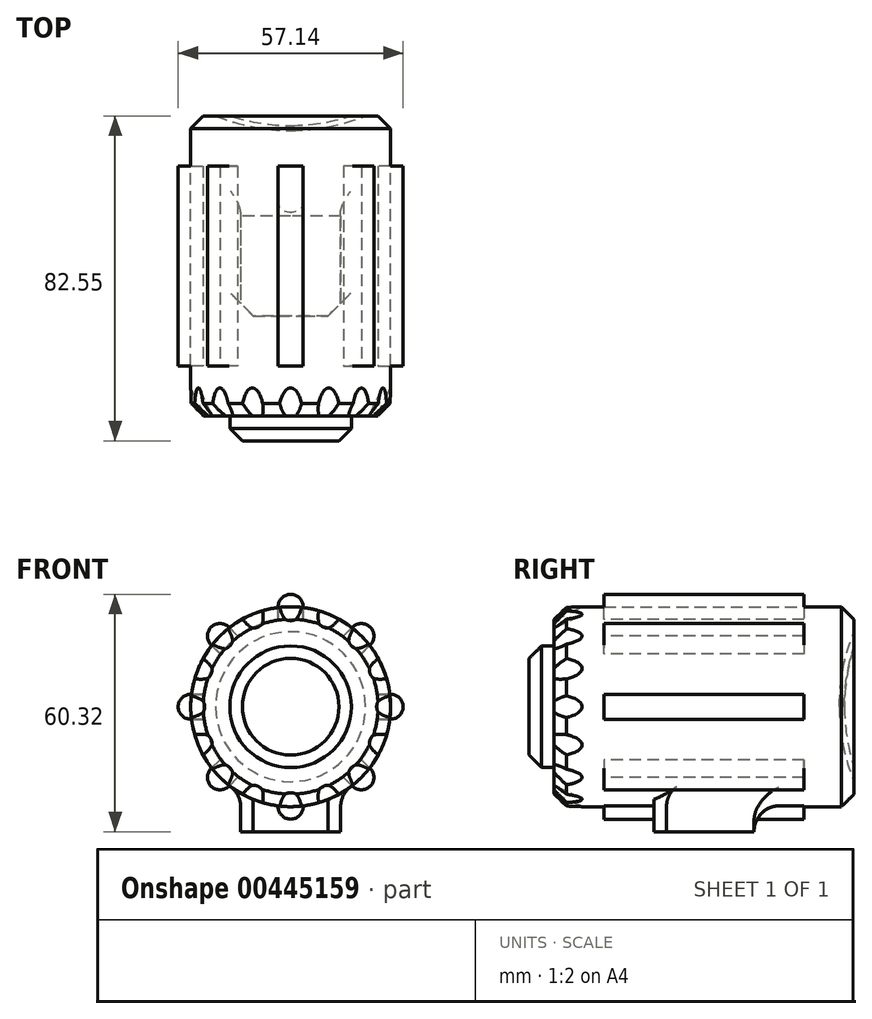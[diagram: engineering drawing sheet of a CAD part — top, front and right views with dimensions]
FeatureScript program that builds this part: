
annotation { "Feature Type Name" : "Feature", "Feature Type Description" : "" }
export const myFeature = defineFeature(function(context is Context, id is Id, definition is map)
    precondition{}
    {
        {
            var Q0;
            Q0=qCreatedBy(makeId("Front.planeOp"),FACE);
            var sketch = newSketch(context, id + "F0", { "sketchPlane" : qUnion([Q0])});
            skCircle(sketch, "E0", {"center": v(0, 0) * mm, "radius": 25.4 * mm});
            skSolve(sketch);
        }
        {
            var Q0;
            Q0=makeQuery(id+"F0.imprint","IMPRINT",FACE,{"disambiguationData":[TD([[makeQuery(id+"F0.imprint","IMPRINT",EDGE,{"derivedFrom":sQuery(id+"F0.wireOp",EDGE,"E0")}),1.0]])]});
            extrude(context, id + "F1", {"entities" : qUnion([Q0]), "depth" : 76.2 * mm});
        }
        {
            var Q0;
            Q0=qCreatedBy(makeId("Right.planeOp"),FACE);
            var sketch = newSketch(context, id + "F2", { "sketchPlane" : qUnion([Q0])});
            skLineSegment(sketch, "E1", {"start": v(-76.2, 25.4) * mm, "end": v(0, 25.4) * mm});
            skLineSegment(sketch, "E2", {"start": v(0, -25.4) * mm, "end": v(-76.2, -25.4) * mm});
            skLineSegment(sketch, "E3", {"start": v(0, 0) * mm, "end": v(0, 22.23) * mm});
            skLineSegment(sketch, "E4", {"start": v(0, 22.23) * mm, "end": v(-3.18, 25.4) * mm});
            skLineSegment(sketch, "E5", {"start": v(0, 0) * mm, "end": v(-8.41, 0) * mm});
            skLineSegment(sketch, "E6", {"start": v(0, 22.23) * mm, "end": v(0, 25.4) * mm});
            skSolve(sketch);
        }
        {
            var Q0;
            {var subQ2=sQuery(id+"F2.wireOp",EDGE,"E4");Q0=makeQuery(id+"F2.imprint","IMPRINT",FACE,{"disambiguationData":[TD([[makeQuery(id+"F2.imprint","IMPRINT",EDGE,{"derivedFrom":subQ2}),-1.0]])]});}
            var Q1;
            Q1=sQuery(id+"F2.wireOp",EDGE,"E5");
            revolve(context, id + "F3", {"operationType" : NewBodyOperationType.REMOVE, "entities" : qUnion([Q0]), "axis" : qUnion([Q1]), "revolveType" : RevolveType.FULL, "oppositeDirection" : true});
        }
        {
            var Q0;
            Q0=qCreatedBy(makeId("Right.planeOp"),FACE);
            var sketch = newSketch(context, id + "F4", { "sketchPlane" : qUnion([Q0])});
            skLineSegment(sketch, "E7", {"start": v(0, 0) * mm, "end": v(-127, 0) * mm});
            skLineSegment(sketch, "E8", {"start": v(-76.2, 25.4) * mm, "end": v(-3.18, 25.4) * mm});
            skLineSegment(sketch, "E9", {"start": v(-127, 0) * mm, "end": v(-76.2, 25.4) * mm});
            skLineSegment(sketch, "E10", {"start": v(-76.2, 25.4) * mm, "end": v(-74.78, 22.56) * mm});
            skLineSegment(sketch, "E11", {"start": v(-74.78, 22.56) * mm, "end": v(-119.9, 0) * mm});
            skLineSegment(sketch, "E12", {"start": v(-74.78, 22.56) * mm, "end": v(-62.33, 28.78) * mm});
            skLineSegment(sketch, "E13", {"start": v(-62.33, 28.78) * mm, "end": v(-63.75, 31.62) * mm});
            skLineSegment(sketch, "E14", {"start": v(-63.75, 31.62) * mm, "end": v(-76.2, 25.4) * mm});
            skSolve(sketch);
        }
        {
            var Q0;
            {var subQ0=sQuery(id+"F4.wireOp",EDGE,"E9");Q0=makeQuery(id+"F4.imprint","IMPRINT",FACE,{"disambiguationData":[TD([[makeQuery(id+"F4.imprint","IMPRINT",EDGE,{"derivedFrom":subQ0}),-1.0]])]});}
            var Q1;
            {var subQ4=sQuery(id+"F4.wireOp",EDGE,"E13");Q1=makeQuery(id+"F4.imprint","IMPRINT",FACE,{"disambiguationData":[TD([[makeQuery(id+"F4.imprint","IMPRINT",EDGE,{"derivedFrom":subQ4}),1.0]])]});}
            var Q2;
            {var subQ0=sQuery(id+"F4.wireOp",EDGE,"E10");Q2=makeQuery(id+"F4.imprint","IMPRINT",FACE,{"disambiguationData":[TD([[makeQuery(id+"F4.imprint","IMPRINT",EDGE,{"derivedFrom":subQ0}),1.0]])]});}
            var Q3;
            Q3=sQuery(id+"F4.wireOp",EDGE,"E9");
            revolve(context, id + "F5", {"entities" : qUnion([Q0, Q1, Q2]), "axis" : qUnion([Q3]), "revolveType" : RevolveType.FULL, "oppositeDirection" : true});
        }
        {
            var Q0;
            Q0=makeQuery(id+"F5.opRevolve","SWEPT_BODY",BODY,{"disambiguationData":[OSD([sQuery(id+"F4.wireOp",EDGE,"E7"),sQuery(id+"F4.wireOp",EDGE,"E9"),sQuery(id+"F4.wireOp",EDGE,"E11"),sQuery(id+"F4.wireOp",EDGE,"E12"),sQuery(id+"F4.wireOp",EDGE,"E13"),sQuery(id+"F4.wireOp",EDGE,"E14")])]});
            var Q1;
            Q1=sQuery(id+"F4.wireOp",EDGE,"E7");
            circularPattern(context, id + "F6", {"operationType" : NewBodyOperationType.REMOVE, "entities" : qUnion([Q0]), "axis" : qUnion([Q1]), "angle" : 360 * degree, "instanceCount" : 16, "equalSpace" : true});
        }
        {
            var Q0;
            Q0=qCreatedBy(makeId("Right.planeOp"),FACE);
            var sketch = newSketch(context, id + "F7", { "sketchPlane" : qUnion([Q0])});
            skLineSegment(sketch, "E15", {"start": v(-3.18, 25.4) * mm, "end": v(0, 22.23) * mm});
            skLineSegment(sketch, "E16", {"start": v(0, -22.23) * mm, "end": v(-3.18, -25.4) * mm});
            skLineSegment(sketch, "E17", {"start": v(0, 22.23) * mm, "end": v(0, 19.05) * mm});
            skArc(sketch, "E18", {"start": v(0, 19.05) * mm, "mid": v(-3.7, 0) * mm, "end": v(0, -19.05) * mm});
            skLineSegment(sketch, "E19", {"start": v(0, -22.23) * mm, "end": v(0, -19.05) * mm});
            skLineSegment(sketch, "E20", {"start": v(0, 19.05) * mm, "end": v(0, -19.05) * mm});
            skLineSegment(sketch, "E21", {"start": v(0, 0) * mm, "end": v(-2.47, 0) * mm});
            skLineSegment(sketch, "E22", {"start": v(0, 19.05) * mm, "end": v(5.56, 19.05) * mm});
            skLineSegment(sketch, "E23", {"start": v(5.56, 19.05) * mm, "end": v(5.56, -19.05) * mm});
            skLineSegment(sketch, "E24", {"start": v(5.56, -19.05) * mm, "end": v(0, -19.05) * mm});
            skLineSegment(sketch, "E25", {"start": v(-3.7, 0) * mm, "end": v(5.56, 0) * mm});
            skSolve(sketch);
        }
        {
            var Q0;
            {var subQ3=sQuery(id+"F7.wireOp",EDGE,"E25");var subQ6=makeQuery(id+"F7.imprint","IMPRINT",VERTEX,{"derivedFrom":subQ3});Q0=makeQuery(id+"F7.imprint","IMPRINT",FACE,{"disambiguationData":[TD([[makeQuery(id+"F7.imprint","IMPRINT",EDGE,{"disambiguationData":[TD([[subQ6,1.0]])],"derivedFrom":subQ3}),1.0]])]});}
            var Q1;
            {var subQ0=sQuery(id+"F7.wireOp",EDGE,"E22");Q1=makeQuery(id+"F7.imprint","IMPRINT",FACE,{"disambiguationData":[TD([[makeQuery(id+"F7.imprint","IMPRINT",EDGE,{"derivedFrom":subQ0}),-1.0]])]});}
            var Q2;
            Q2=sQuery(id+"F7.wireOp",EDGE,"E25");
            revolve(context, id + "F8", {"operationType" : NewBodyOperationType.REMOVE, "entities" : qUnion([Q0, Q1]), "axis" : qUnion([Q2]), "revolveType" : RevolveType.FULL, "oppositeDirection" : true});
        }
        {
            var Q0;
            Q0=qCreatedBy(makeId("Right.planeOp"),FACE);
            var sketch = newSketch(context, id + "F9", { "sketchPlane" : qUnion([Q0])});
            skLineSegment(sketch, "E26.0", {"start": v(0, 19.05) * mm, "end": v(0, -19.05) * mm});
            skArc(sketch, "E27", {"start": v(0, 19.05) * mm, "mid": v(-3.7, 0) * mm, "end": v(0, -19.05) * mm});
            skArc(sketch, "E28", {"start": v(0, 15.35) * mm, "mid": v(-2.44, 0) * mm, "end": v(0, -15.35) * mm});
            skLineSegment(sketch, "E29", {"start": v(0, 19.05) * mm, "end": v(0, 15.35) * mm});
            skLineSegment(sketch, "E30", {"start": v(0, -19.05) * mm, "end": v(0, -15.35) * mm});
            skLineSegment(sketch, "E31", {"start": v(0, 0) * mm, "end": v(-3.7, 0) * mm});
            skArc(sketch, "E32", {"start": v(-0.15, 14.89) * mm, "mid": v(-0.04, 15.36) * mm, "end": v(0, 15.84) * mm});
            skSolve(sketch);
        }
        {
            var Q0;
            {var subQ5=sQuery(id+"F9.wireOp",EDGE,"E32");Q0=makeQuery(id+"F9.imprint","IMPRINT",FACE,{"disambiguationData":[TD([[makeQuery(id+"F9.imprint","IMPRINT",EDGE,{"derivedFrom":subQ5}),1.0]])]});}
            var Q1;
            Q1=sQuery(id+"F9.wireOp",EDGE,"E31");
            revolve(context, id + "F10", {"entities" : qUnion([Q0]), "axis" : qUnion([Q1]), "revolveType" : RevolveType.FULL});
        }
        {
            var Q0;
            {var subQ0=sQuery(id+"F0.wireOp",EDGE,"E0");var subQ1=makeQuery(id+"F5.opRevolve","SWEPT_FACE",FACE,{"disambiguationData":[OSD([sQuery(id+"F4.wireOp",EDGE,"E11"),sQuery(id+"F4.wireOp",EDGE,"E12")])]});Q0=makeQuery(id+"F6.boolean.opBoolean","SPLIT",EDGE,{"disambiguationData":[TD([makeQuery(id+"F1.opExtrude","SWEPT_FACE",FACE,{"disambiguationData":[OSD([subQ0])]}),makeQuery(id+"F1.opExtrude","CAP_FACE",FACE,{"disambiguationData":[OSD([subQ0])],"isStart":false}),makeQuery(id+"F6.opPattern","COPY",FACE,{"derivedFrom":subQ1,"instanceName":"13"}),makeQuery(id+"F6.opPattern","COPY",FACE,{"derivedFrom":subQ1,"instanceName":"14"})])],"derivedFrom":makeQuery(id+"F1.opExtrude","CAP_EDGE",EDGE,{"disambiguationData":[OSD([subQ0])],"isStart":false})});}
            var Q1;
            {var subQ0=sQuery(id+"F0.wireOp",EDGE,"E0");var subQ1=makeQuery(id+"F5.opRevolve","SWEPT_FACE",FACE,{"disambiguationData":[OSD([sQuery(id+"F4.wireOp",EDGE,"E11"),sQuery(id+"F4.wireOp",EDGE,"E12")])]});Q1=makeQuery(id+"F6.boolean.opBoolean","SPLIT",EDGE,{"disambiguationData":[TD([makeQuery(id+"F1.opExtrude","SWEPT_FACE",FACE,{"disambiguationData":[OSD([subQ0])]}),makeQuery(id+"F1.opExtrude","CAP_FACE",FACE,{"disambiguationData":[OSD([subQ0])],"isStart":false}),makeQuery(id+"F6.opPattern","COPY",FACE,{"derivedFrom":subQ1,"instanceName":"12"}),makeQuery(id+"F6.opPattern","COPY",FACE,{"derivedFrom":subQ1,"instanceName":"13"})])],"derivedFrom":makeQuery(id+"F1.opExtrude","CAP_EDGE",EDGE,{"disambiguationData":[OSD([subQ0])],"isStart":false})});}
            var Q2;
            {var subQ0=sQuery(id+"F0.wireOp",EDGE,"E0");var subQ1=makeQuery(id+"F5.opRevolve","SWEPT_FACE",FACE,{"disambiguationData":[OSD([sQuery(id+"F4.wireOp",EDGE,"E11"),sQuery(id+"F4.wireOp",EDGE,"E12")])]});Q2=makeQuery(id+"F6.boolean.opBoolean","SPLIT",EDGE,{"disambiguationData":[TD([makeQuery(id+"F1.opExtrude","SWEPT_FACE",FACE,{"disambiguationData":[OSD([subQ0])]}),makeQuery(id+"F1.opExtrude","CAP_FACE",FACE,{"disambiguationData":[OSD([subQ0])],"isStart":false}),makeQuery(id+"F6.opPattern","COPY",FACE,{"derivedFrom":subQ1,"instanceName":"11"}),makeQuery(id+"F6.opPattern","COPY",FACE,{"derivedFrom":subQ1,"instanceName":"12"})])],"derivedFrom":makeQuery(id+"F1.opExtrude","CAP_EDGE",EDGE,{"disambiguationData":[OSD([subQ0])],"isStart":false})});}
            var Q3;
            {var subQ0=sQuery(id+"F0.wireOp",EDGE,"E0");var subQ1=makeQuery(id+"F5.opRevolve","SWEPT_FACE",FACE,{"disambiguationData":[OSD([sQuery(id+"F4.wireOp",EDGE,"E11"),sQuery(id+"F4.wireOp",EDGE,"E12")])]});Q3=makeQuery(id+"F6.boolean.opBoolean","SPLIT",EDGE,{"disambiguationData":[TD([makeQuery(id+"F1.opExtrude","SWEPT_FACE",FACE,{"disambiguationData":[OSD([subQ0])]}),makeQuery(id+"F1.opExtrude","CAP_FACE",FACE,{"disambiguationData":[OSD([subQ0])],"isStart":false}),makeQuery(id+"F6.opPattern","COPY",FACE,{"derivedFrom":subQ1,"instanceName":"10"}),makeQuery(id+"F6.opPattern","COPY",FACE,{"derivedFrom":subQ1,"instanceName":"11"})])],"derivedFrom":makeQuery(id+"F1.opExtrude","CAP_EDGE",EDGE,{"disambiguationData":[OSD([subQ0])],"isStart":false})});}
            var Q4;
            {var subQ0=sQuery(id+"F0.wireOp",EDGE,"E0");var subQ1=makeQuery(id+"F5.opRevolve","SWEPT_FACE",FACE,{"disambiguationData":[OSD([sQuery(id+"F4.wireOp",EDGE,"E11"),sQuery(id+"F4.wireOp",EDGE,"E12")])]});Q4=makeQuery(id+"F6.boolean.opBoolean","SPLIT",EDGE,{"disambiguationData":[TD([makeQuery(id+"F1.opExtrude","SWEPT_FACE",FACE,{"disambiguationData":[OSD([subQ0])]}),makeQuery(id+"F1.opExtrude","CAP_FACE",FACE,{"disambiguationData":[OSD([subQ0])],"isStart":false}),makeQuery(id+"F6.opPattern","COPY",FACE,{"derivedFrom":subQ1,"instanceName":"9"}),makeQuery(id+"F6.opPattern","COPY",FACE,{"derivedFrom":subQ1,"instanceName":"10"})])],"derivedFrom":makeQuery(id+"F1.opExtrude","CAP_EDGE",EDGE,{"disambiguationData":[OSD([subQ0])],"isStart":false})});}
            var Q5;
            {var subQ0=sQuery(id+"F0.wireOp",EDGE,"E0");var subQ1=makeQuery(id+"F5.opRevolve","SWEPT_FACE",FACE,{"disambiguationData":[OSD([sQuery(id+"F4.wireOp",EDGE,"E11"),sQuery(id+"F4.wireOp",EDGE,"E12")])]});Q5=makeQuery(id+"F6.boolean.opBoolean","SPLIT",EDGE,{"disambiguationData":[TD([makeQuery(id+"F1.opExtrude","SWEPT_FACE",FACE,{"disambiguationData":[OSD([subQ0])]}),makeQuery(id+"F1.opExtrude","CAP_FACE",FACE,{"disambiguationData":[OSD([subQ0])],"isStart":false}),makeQuery(id+"F6.opPattern","COPY",FACE,{"derivedFrom":subQ1,"instanceName":"8"}),makeQuery(id+"F6.opPattern","COPY",FACE,{"derivedFrom":subQ1,"instanceName":"9"})])],"derivedFrom":makeQuery(id+"F1.opExtrude","CAP_EDGE",EDGE,{"disambiguationData":[OSD([subQ0])],"isStart":false})});}
            var Q6;
            {var subQ0=sQuery(id+"F0.wireOp",EDGE,"E0");var subQ1=makeQuery(id+"F5.opRevolve","SWEPT_FACE",FACE,{"disambiguationData":[OSD([sQuery(id+"F4.wireOp",EDGE,"E11"),sQuery(id+"F4.wireOp",EDGE,"E12")])]});Q6=makeQuery(id+"F6.boolean.opBoolean","SPLIT",EDGE,{"disambiguationData":[TD([makeQuery(id+"F1.opExtrude","SWEPT_FACE",FACE,{"disambiguationData":[OSD([subQ0])]}),makeQuery(id+"F1.opExtrude","CAP_FACE",FACE,{"disambiguationData":[OSD([subQ0])],"isStart":false}),makeQuery(id+"F6.opPattern","COPY",FACE,{"derivedFrom":subQ1,"instanceName":"7"}),makeQuery(id+"F6.opPattern","COPY",FACE,{"derivedFrom":subQ1,"instanceName":"8"})])],"derivedFrom":makeQuery(id+"F1.opExtrude","CAP_EDGE",EDGE,{"disambiguationData":[OSD([subQ0])],"isStart":false})});}
            var Q7;
            {var subQ0=sQuery(id+"F0.wireOp",EDGE,"E0");var subQ1=makeQuery(id+"F5.opRevolve","SWEPT_FACE",FACE,{"disambiguationData":[OSD([sQuery(id+"F4.wireOp",EDGE,"E11"),sQuery(id+"F4.wireOp",EDGE,"E12")])]});Q7=makeQuery(id+"F6.boolean.opBoolean","SPLIT",EDGE,{"disambiguationData":[TD([makeQuery(id+"F1.opExtrude","SWEPT_FACE",FACE,{"disambiguationData":[OSD([subQ0])]}),makeQuery(id+"F1.opExtrude","CAP_FACE",FACE,{"disambiguationData":[OSD([subQ0])],"isStart":false}),makeQuery(id+"F6.opPattern","COPY",FACE,{"derivedFrom":subQ1,"instanceName":"6"}),makeQuery(id+"F6.opPattern","COPY",FACE,{"derivedFrom":subQ1,"instanceName":"7"})])],"derivedFrom":makeQuery(id+"F1.opExtrude","CAP_EDGE",EDGE,{"disambiguationData":[OSD([subQ0])],"isStart":false})});}
            var Q8;
            {var subQ0=sQuery(id+"F0.wireOp",EDGE,"E0");var subQ1=makeQuery(id+"F5.opRevolve","SWEPT_FACE",FACE,{"disambiguationData":[OSD([sQuery(id+"F4.wireOp",EDGE,"E11"),sQuery(id+"F4.wireOp",EDGE,"E12")])]});Q8=makeQuery(id+"F6.boolean.opBoolean","SPLIT",EDGE,{"disambiguationData":[TD([makeQuery(id+"F1.opExtrude","SWEPT_FACE",FACE,{"disambiguationData":[OSD([subQ0])]}),makeQuery(id+"F1.opExtrude","CAP_FACE",FACE,{"disambiguationData":[OSD([subQ0])],"isStart":false}),makeQuery(id+"F6.opPattern","COPY",FACE,{"derivedFrom":subQ1,"instanceName":"5"}),makeQuery(id+"F6.opPattern","COPY",FACE,{"derivedFrom":subQ1,"instanceName":"6"})])],"derivedFrom":makeQuery(id+"F1.opExtrude","CAP_EDGE",EDGE,{"disambiguationData":[OSD([subQ0])],"isStart":false})});}
            var Q9;
            {var subQ0=sQuery(id+"F0.wireOp",EDGE,"E0");var subQ1=makeQuery(id+"F5.opRevolve","SWEPT_FACE",FACE,{"disambiguationData":[OSD([sQuery(id+"F4.wireOp",EDGE,"E11"),sQuery(id+"F4.wireOp",EDGE,"E12")])]});Q9=makeQuery(id+"F6.boolean.opBoolean","SPLIT",EDGE,{"disambiguationData":[TD([makeQuery(id+"F1.opExtrude","SWEPT_FACE",FACE,{"disambiguationData":[OSD([subQ0])]}),makeQuery(id+"F1.opExtrude","CAP_FACE",FACE,{"disambiguationData":[OSD([subQ0])],"isStart":false}),makeQuery(id+"F6.opPattern","COPY",FACE,{"derivedFrom":subQ1,"instanceName":"4"}),makeQuery(id+"F6.opPattern","COPY",FACE,{"derivedFrom":subQ1,"instanceName":"5"})])],"derivedFrom":makeQuery(id+"F1.opExtrude","CAP_EDGE",EDGE,{"disambiguationData":[OSD([subQ0])],"isStart":false})});}
            var Q10;
            {var subQ0=sQuery(id+"F0.wireOp",EDGE,"E0");var subQ1=makeQuery(id+"F5.opRevolve","SWEPT_FACE",FACE,{"disambiguationData":[OSD([sQuery(id+"F4.wireOp",EDGE,"E11"),sQuery(id+"F4.wireOp",EDGE,"E12")])]});Q10=makeQuery(id+"F6.boolean.opBoolean","SPLIT",EDGE,{"disambiguationData":[TD([makeQuery(id+"F1.opExtrude","SWEPT_FACE",FACE,{"disambiguationData":[OSD([subQ0])]}),makeQuery(id+"F1.opExtrude","CAP_FACE",FACE,{"disambiguationData":[OSD([subQ0])],"isStart":false}),makeQuery(id+"F6.opPattern","COPY",FACE,{"derivedFrom":subQ1,"instanceName":"3"}),makeQuery(id+"F6.opPattern","COPY",FACE,{"derivedFrom":subQ1,"instanceName":"4"})])],"derivedFrom":makeQuery(id+"F1.opExtrude","CAP_EDGE",EDGE,{"disambiguationData":[OSD([subQ0])],"isStart":false})});}
            var Q11;
            {var subQ0=sQuery(id+"F0.wireOp",EDGE,"E0");var subQ1=makeQuery(id+"F5.opRevolve","SWEPT_FACE",FACE,{"disambiguationData":[OSD([sQuery(id+"F4.wireOp",EDGE,"E11"),sQuery(id+"F4.wireOp",EDGE,"E12")])]});Q11=makeQuery(id+"F6.boolean.opBoolean","SPLIT",EDGE,{"disambiguationData":[TD([makeQuery(id+"F1.opExtrude","SWEPT_FACE",FACE,{"disambiguationData":[OSD([subQ0])]}),makeQuery(id+"F1.opExtrude","CAP_FACE",FACE,{"disambiguationData":[OSD([subQ0])],"isStart":false}),makeQuery(id+"F6.opPattern","COPY",FACE,{"derivedFrom":subQ1,"instanceName":"2"}),makeQuery(id+"F6.opPattern","COPY",FACE,{"derivedFrom":subQ1,"instanceName":"3"})])],"derivedFrom":makeQuery(id+"F1.opExtrude","CAP_EDGE",EDGE,{"disambiguationData":[OSD([subQ0])],"isStart":false})});}
            var Q12;
            {var subQ0=sQuery(id+"F0.wireOp",EDGE,"E0");var subQ1=makeQuery(id+"F5.opRevolve","SWEPT_FACE",FACE,{"disambiguationData":[OSD([sQuery(id+"F4.wireOp",EDGE,"E11"),sQuery(id+"F4.wireOp",EDGE,"E12")])]});Q12=makeQuery(id+"F6.boolean.opBoolean","SPLIT",EDGE,{"disambiguationData":[TD([makeQuery(id+"F1.opExtrude","SWEPT_FACE",FACE,{"disambiguationData":[OSD([subQ0])]}),makeQuery(id+"F1.opExtrude","CAP_FACE",FACE,{"disambiguationData":[OSD([subQ0])],"isStart":false}),makeQuery(id+"F6.opPattern","COPY",FACE,{"derivedFrom":subQ1,"instanceName":"1"}),makeQuery(id+"F6.opPattern","COPY",FACE,{"derivedFrom":subQ1,"instanceName":"2"})])],"derivedFrom":makeQuery(id+"F1.opExtrude","CAP_EDGE",EDGE,{"disambiguationData":[OSD([subQ0])],"isStart":false})});}
            var Q13;
            {var subQ0=sQuery(id+"F0.wireOp",EDGE,"E0");var subQ1=makeQuery(id+"F5.opRevolve","SWEPT_FACE",FACE,{"disambiguationData":[OSD([sQuery(id+"F4.wireOp",EDGE,"E11"),sQuery(id+"F4.wireOp",EDGE,"E12")])]});Q13=makeQuery(id+"F6.boolean.opBoolean","SPLIT",EDGE,{"disambiguationData":[TD([makeQuery(id+"F1.opExtrude","SWEPT_FACE",FACE,{"disambiguationData":[OSD([subQ0])]}),makeQuery(id+"F1.opExtrude","CAP_FACE",FACE,{"disambiguationData":[OSD([subQ0])],"isStart":false}),subQ1,makeQuery(id+"F6.opPattern","COPY",FACE,{"derivedFrom":subQ1,"instanceName":"1"})])],"derivedFrom":makeQuery(id+"F1.opExtrude","CAP_EDGE",EDGE,{"disambiguationData":[OSD([subQ0])],"isStart":false})});}
            var Q14;
            {var subQ0=sQuery(id+"F0.wireOp",EDGE,"E0");var subQ1=makeQuery(id+"F5.opRevolve","SWEPT_FACE",FACE,{"disambiguationData":[OSD([sQuery(id+"F4.wireOp",EDGE,"E11"),sQuery(id+"F4.wireOp",EDGE,"E12")])]});Q14=makeQuery(id+"F6.boolean.opBoolean","SPLIT",EDGE,{"disambiguationData":[TD([makeQuery(id+"F1.opExtrude","SWEPT_FACE",FACE,{"disambiguationData":[OSD([subQ0])]}),makeQuery(id+"F1.opExtrude","CAP_FACE",FACE,{"disambiguationData":[OSD([subQ0])],"isStart":false}),subQ1,makeQuery(id+"F6.opPattern","COPY",FACE,{"derivedFrom":subQ1,"instanceName":"15"})])],"derivedFrom":makeQuery(id+"F1.opExtrude","CAP_EDGE",EDGE,{"disambiguationData":[OSD([subQ0])],"isStart":false})});}
            var Q15;
            {var subQ0=sQuery(id+"F0.wireOp",EDGE,"E0");var subQ1=makeQuery(id+"F5.opRevolve","SWEPT_FACE",FACE,{"disambiguationData":[OSD([sQuery(id+"F4.wireOp",EDGE,"E11"),sQuery(id+"F4.wireOp",EDGE,"E12")])]});Q15=makeQuery(id+"F6.boolean.opBoolean","SPLIT",EDGE,{"disambiguationData":[TD([makeQuery(id+"F1.opExtrude","SWEPT_FACE",FACE,{"disambiguationData":[OSD([subQ0])]}),makeQuery(id+"F1.opExtrude","CAP_FACE",FACE,{"disambiguationData":[OSD([subQ0])],"isStart":false}),makeQuery(id+"F6.opPattern","COPY",FACE,{"derivedFrom":subQ1,"instanceName":"14"}),makeQuery(id+"F6.opPattern","COPY",FACE,{"derivedFrom":subQ1,"instanceName":"15"})])],"derivedFrom":makeQuery(id+"F1.opExtrude","CAP_EDGE",EDGE,{"disambiguationData":[OSD([subQ0])],"isStart":false})});}
            chamfer(context, id + "F11", {"entities" : qUnion([Q0, Q1, Q2, Q3, Q4, Q5, Q6, Q7, Q8, Q9, Q10, Q11, Q12, Q13, Q14, Q15]), "width" : 3.17 * mm, "tangentPropagation" : true});
        }
        {
            var Q0;
            Q0=qCreatedBy(makeId("Right.planeOp"),FACE);
            var sketch = newSketch(context, id + "F12", { "sketchPlane" : qUnion([Q0])});
            skFitSpline(sketch, "E33.0.0", {"points": [v(-76.2, 21.8) * mm, v(-76.2, 20.51) * mm, v(-76.2, 19.23) * mm, v(-76.2, 17.94) * mm]});
            skFitSpline(sketch, "E33.0.7", {"points": [v(-76.2, -21.8) * mm, v(-76.2, -21.16) * mm, v(-76.2, -20.52) * mm, v(-76.2, -19.89) * mm]});
            skFitSpline(sketch, "E33.0.15", {"points": [v(-76.2, 21.8) * mm, v(-76.2, 21.16) * mm, v(-76.2, 20.52) * mm, v(-76.2, 19.89) * mm]});
            skLineSegment(sketch, "E34", {"start": v(-76.2, -21.8) * mm, "end": v(-76.2, 21.8) * mm});
            skLineSegment(sketch, "E35", {"start": v(-76.2, 21.8) * mm, "end": v(-76.2, 15.45) * mm});
            skLineSegment(sketch, "E36", {"start": v(-76.2, -21.8) * mm, "end": v(-76.2, -15.45) * mm});
            skLineSegment(sketch, "E37", {"start": v(-76.2, -15.45) * mm, "end": v(-82.55, -15.45) * mm});
            skLineSegment(sketch, "E38", {"start": v(-76.2, 15.45) * mm, "end": v(-82.55, 15.45) * mm});
            skLineSegment(sketch, "E39", {"start": v(-82.55, 15.45) * mm, "end": v(-82.55, -15.45) * mm});
            skLineSegment(sketch, "E40", {"start": v(-82.55, 0) * mm, "end": v(-76.2, 0) * mm});
            skSolve(sketch);
        }
        {
            var Q0;
            {var subQ0=sQuery(id+"F12.wireOp",EDGE,"E38");Q0=makeQuery(id+"F12.imprint","IMPRINT",FACE,{"disambiguationData":[TD([[makeQuery(id+"F12.imprint","IMPRINT",EDGE,{"derivedFrom":subQ0}),1.0]])]});}
            var Q1;
            Q1=sQuery(id+"F12.wireOp",EDGE,"E40");
            revolve(context, id + "F13", {"entities" : qUnion([Q0]), "axis" : qUnion([Q1]), "revolveType" : RevolveType.FULL});
        }
        {
            var Q0;
            Q0=makeQuery(id+"F13.opRevolve","SWEPT_FACE",FACE,{"disambiguationData":[OSD([sQuery(id+"F12.wireOp",EDGE,"E39")])]});
            chamfer(context, id + "F14", {"entities" : qUnion([Q0]), "width" : 3.17 * mm, "tangentPropagation" : true});
        }
        {
            var Q0;
            Q0=qCreatedBy(makeId("Right.planeOp"),FACE);
            var sketch = newSketch(context, id + "F15", { "sketchPlane" : qUnion([Q0])});
            skLineSegment(sketch, "E41", {"start": v(0, 0) * mm, "end": v(0, 25.4) * mm});
            skLineSegment(sketch, "E42", {"start": v(0, 25.4) * mm, "end": v(-12.7, 25.4) * mm});
            skLineSegment(sketch, "E43", {"start": v(-12.7, 25.4) * mm, "end": v(-12.7, 22.22) * mm});
            skLineSegment(sketch, "E44", {"start": v(-12.7, 22.22) * mm, "end": v(-63.5, 22.22) * mm});
            skLineSegment(sketch, "E45", {"start": v(-63.5, 22.22) * mm, "end": v(-63.5, 28.57) * mm});
            skLineSegment(sketch, "E46", {"start": v(-63.5, 28.57) * mm, "end": v(-12.7, 28.58) * mm});
            skLineSegment(sketch, "E47", {"start": v(-12.7, 28.58) * mm, "end": v(-12.7, 25.4) * mm});
            skSolve(sketch);
        }
        {
            var Q0;
            Q0=makeQuery(id+"F15.imprint","IMPRINT",FACE,{"disambiguationData":[TD([[makeQuery(id+"F15.imprint","IMPRINT",EDGE,{"derivedFrom":sQuery(id+"F15.wireOp",EDGE,"E43")}),-1.0]])]});
            extrude(context, id + "F16", {"entities" : qUnion([Q0]), "endBound" : BoundingType.SYMMETRIC, "depth" : 6.35 * mm});
        }
        {
            var Q0;
            Q0=makeQuery(id+"F16.opExtrude","CAP_EDGE",EDGE,{"disambiguationData":[OSD([sQuery(id+"F15.wireOp",EDGE,"E46")])],"isStart":false});
            var Q1;
            Q1=makeQuery(id+"F16.opExtrude","CAP_EDGE",EDGE,{"disambiguationData":[OSD([sQuery(id+"F15.wireOp",EDGE,"E46")])],"isStart":true});
            fillet(context, id + "F17", {"entities" : qUnion([Q0, Q1]), "radius" : 3.17 * mm, "tangentPropagation" : true, "allowEdgeOverflow" : false});
        }
        {
            var Q0;
            Q0=makeQuery(id+"F16.opExtrude","SWEPT_BODY",BODY,{"disambiguationData":[OSD([sQuery(id+"F15.wireOp",EDGE,"E43"),sQuery(id+"F15.wireOp",EDGE,"E44"),sQuery(id+"F15.wireOp",EDGE,"E45"),sQuery(id+"F15.wireOp",EDGE,"E46"),sQuery(id+"F15.wireOp",EDGE,"E47")])]});
            var Q1;
            Q1=sQuery(id+"F12.wireOp",EDGE,"E40");
            circularPattern(context, id + "F18", {"entities" : qUnion([Q0]), "axis" : qUnion([Q1]), "angle" : 360 * degree, "instanceCount" : 8, "equalSpace" : true});
        }
        {
            var Q0;
            Q0=qCreatedBy(makeId("Right.planeOp"),FACE);
            var sketch = newSketch(context, id + "F19", { "sketchPlane" : qUnion([Q0])});
            skLineSegment(sketch, "E48", {"start": v(0, 0) * mm, "end": v(-25.4, 0) * mm});
            skLineSegment(sketch, "E49", {"start": v(-25.4, 0) * mm, "end": v(-25.4, -31.75) * mm});
            skLineSegment(sketch, "E50", {"start": v(-25.4, -31.75) * mm, "end": v(-50.8, -31.75) * mm});
            skLineSegment(sketch, "E51", {"start": v(-50.8, -31.75) * mm, "end": v(-50.8, 0) * mm});
            skLineSegment(sketch, "E52", {"start": v(-50.8, 0) * mm, "end": v(-25.4, 0) * mm});
            skSolve(sketch);
        }
        {
            var Q0;
            Q0=makeQuery(id+"F19.imprint","IMPRINT",FACE,{"disambiguationData":[TD([[makeQuery(id+"F19.imprint","IMPRINT",EDGE,{"derivedFrom":sQuery(id+"F19.wireOp",EDGE,"E49")}),-1.0]])]});
            extrude(context, id + "F20", {"entities" : qUnion([Q0]), "operationType" : NewBodyOperationType.ADD, "endBound" : BoundingType.SYMMETRIC, "depth" : 25.4 * mm});
        }
        {
            var Q0;
            Q0=makeQuery(id+"F20.opExtrude","CAP_EDGE",EDGE,{"disambiguationData":[OSD([sQuery(id+"F19.wireOp",EDGE,"E51")])],"isStart":true});
            var Q1;
            Q1=makeQuery(id+"F20.opExtrude","CAP_EDGE",EDGE,{"disambiguationData":[OSD([sQuery(id+"F19.wireOp",EDGE,"E51")])],"isStart":false});
            chamfer(context, id + "F21", {"entities" : qUnion([Q0, Q1]), "width" : 3.17 * mm, "tangentPropagation" : true});
        }
        {
            var Q0;
            Q0=makeQuery(id+"F20.boolean.opBoolean","INTERSECT",EDGE,{"derivedFrom":[makeQuery(id+"F1.opExtrude","SWEPT_FACE",FACE,{"disambiguationData":[OSD([sQuery(id+"F0.wireOp",EDGE,"E0")])]}),makeQuery(id+"F20.opExtrude","CAP_FACE",FACE,{"disambiguationData":[OSD([sQuery(id+"F19.wireOp",EDGE,"E49"),sQuery(id+"F19.wireOp",EDGE,"E50"),sQuery(id+"F19.wireOp",EDGE,"E51"),sQuery(id+"F19.wireOp",EDGE,"E52")])],"isStart":false})]});
            var Q1;
            Q1=makeQuery(id+"F20.boolean.opBoolean","INTERSECT",EDGE,{"derivedFrom":[makeQuery(id+"F1.opExtrude","SWEPT_FACE",FACE,{"disambiguationData":[OSD([sQuery(id+"F0.wireOp",EDGE,"E0")])]}),makeQuery(id+"F20.opExtrude","CAP_FACE",FACE,{"disambiguationData":[OSD([sQuery(id+"F19.wireOp",EDGE,"E49"),sQuery(id+"F19.wireOp",EDGE,"E50"),sQuery(id+"F19.wireOp",EDGE,"E51"),sQuery(id+"F19.wireOp",EDGE,"E52")])],"isStart":true})]});
            var Q2;
            Q2=makeQuery(id+"F20.boolean.opBoolean","INTERSECT",EDGE,{"disambiguationData":[OD(1.0)],"derivedFrom":[makeQuery(id+"F1.opExtrude","SWEPT_FACE",FACE,{"disambiguationData":[OSD([sQuery(id+"F0.wireOp",EDGE,"E0")])]}),makeQuery(id+"F20.opExtrude","SWEPT_FACE",FACE,{"disambiguationData":[OSD([sQuery(id+"F19.wireOp",EDGE,"E49")])]})]});
            var Q3;
            Q3=makeQuery(id+"F20.boolean.opBoolean","INTERSECT",EDGE,{"disambiguationData":[OD(0.0)],"derivedFrom":[makeQuery(id+"F1.opExtrude","SWEPT_FACE",FACE,{"disambiguationData":[OSD([sQuery(id+"F0.wireOp",EDGE,"E0")])]}),makeQuery(id+"F20.opExtrude","SWEPT_FACE",FACE,{"disambiguationData":[OSD([sQuery(id+"F19.wireOp",EDGE,"E49")])]})]});
            fillet(context, id + "F22", {"entities" : qUnion([Q0, Q1, Q2, Q3]), "radius" : 6.35 * mm, "tangentPropagation" : true, "allowEdgeOverflow" : false});
        }
    });
